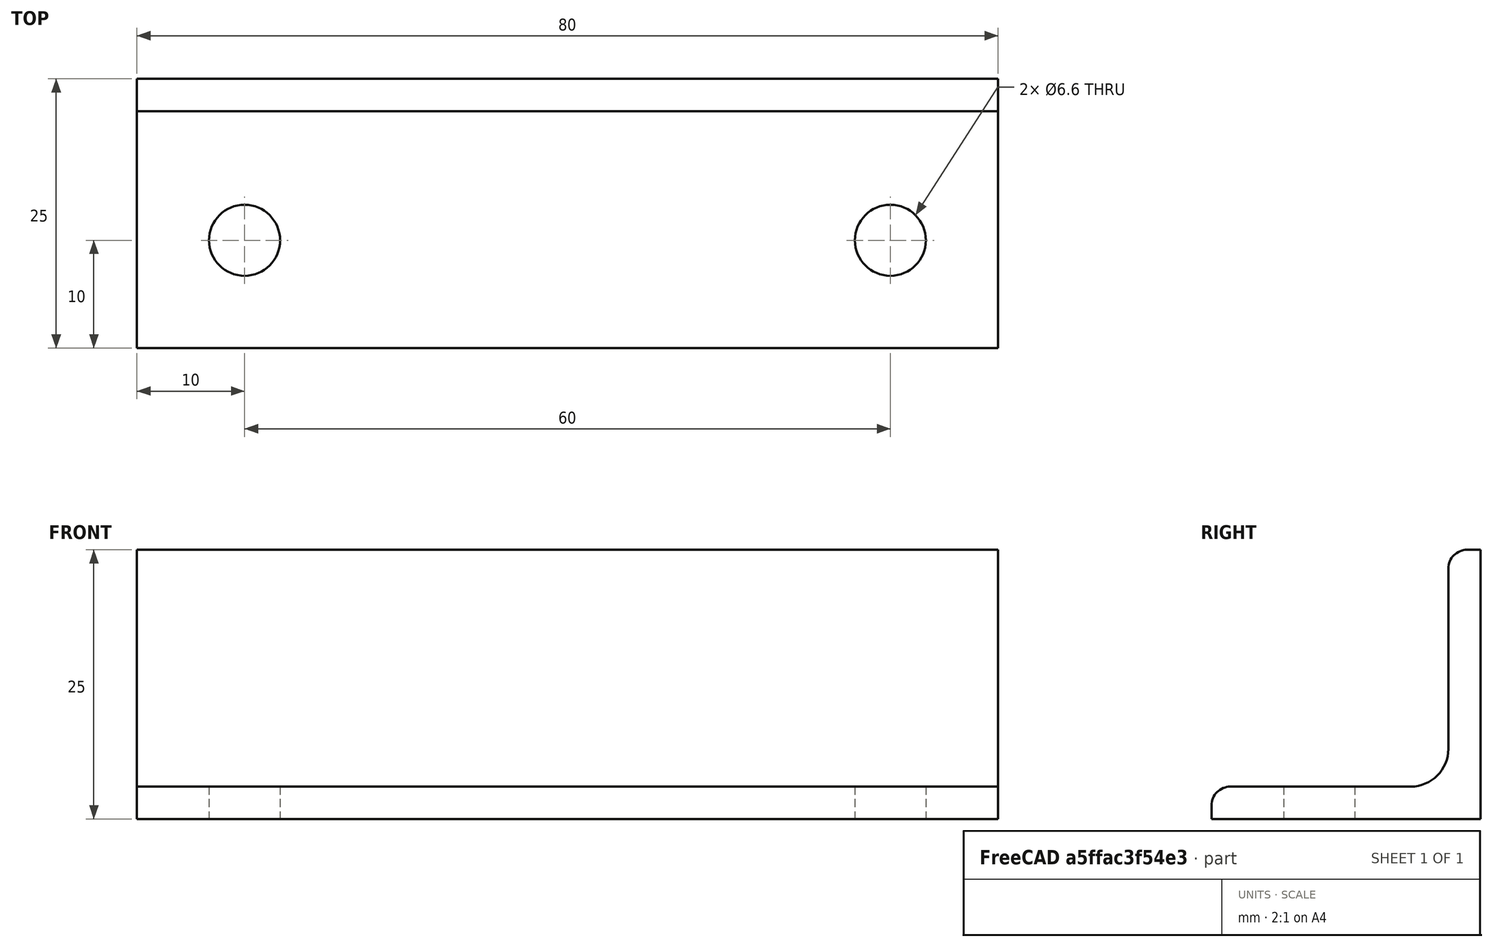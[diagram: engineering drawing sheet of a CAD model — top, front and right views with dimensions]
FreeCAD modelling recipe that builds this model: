
FCSTD DOCUMENT  (FreeCAD 1.0R39319 (Git))
Label: OCT-CHBRA-AC
License: Creative Commons Attribution 4.0
LicenseURL: https://creativecommons.org/licenses/by/4.0/
objects: TechDraw::DrawViewDimension×9, TechDraw::DrawProjGroupItem×3, Sketcher::SketchObject×2, PartDesign::Pad×1, PartDesign::Hole×1, PartDesign::Body×1, TechDraw::DrawSVGTemplate×1, TechDraw::DrawProjGroup×1, TechDraw::DrawPage×1
note: 25 computed .brp shape members not serialized (recipe doc carries the construction recipe); baked Part::Feature solids carry a one-line shape summary decoded from their .brp

FEATURE [Sketcher::SketchObject] Sketch
  ArcFitTolerance = 1e-06
  AttachmentSupport = -> [YZ_Plane001]
  FullyConstrained = true
  MakeInternals = false
  MapMode = 5
  Placement = pos=(0,0,0) rot=(0.57735,0.57735,0.57735;2.0944rad)
  sketch-geometry (9):
    g0: LineSegment StartX=0 StartY=25 StartZ=0 EndX=0 EndY=0 EndZ=0
    g1: LineSegment StartX=0 StartY=0 StartZ=0 EndX=-25 EndY=0 EndZ=0
    g2: ArcOfCircle CenterX=-6.5 CenterY=6.5 CenterZ=0 NormalX=0 NormalY=0 NormalZ=1 AngleXU=0 Radius=3.5 StartAngle=4.71239 EndAngle=6.28319
    g3: LineSegment StartX=-23.25 StartY=3 StartZ=0 EndX=-6.5 EndY=3 EndZ=0
    g4: LineSegment StartX=-3 StartY=6.5 StartZ=0 EndX=-3 EndY=23.25 EndZ=0
    g5: LineSegment StartX=0 StartY=25 StartZ=0 EndX=-1.25 EndY=25 EndZ=0
    g6: ArcOfCircle CenterX=-1.25 CenterY=23.25 CenterZ=0 NormalX=0 NormalY=0 NormalZ=1 AngleXU=0 Radius=1.75 StartAngle=1.5708 EndAngle=3.14159
    g7: LineSegment StartX=-25 StartY=0 StartZ=0 EndX=-25 EndY=1.25 EndZ=0
    g8: ArcOfCircle CenterX=-23.25 CenterY=1.25 CenterZ=0 NormalX=0 NormalY=0 NormalZ=1 AngleXU=0 Radius=1.75 StartAngle=1.5708 EndAngle=3.14159
  constraints (23):
    c: PointOnObject(g0,g-2)
    c: Coincident(g0,g-1)
    c: Coincident(g0,g1)
    c: PointOnObject(g1,g-1)
    c: Vertical(g4)
    c: Horizontal(g3)
    c: Tangent(g3,g2) = -1.5708
    c: Tangent(g4,g2) = -1.5708
    c: DistanceY(g0,g0) = 25
    c: Equal(g0,g1)
    c: Radius(g2) = 3.5
    c: Coincident(g0,g5)
    c: Horizontal(g5)
    c: Tangent(g5,g6) = -1.5708
    c: Coincident(g1,g7)
    c: Vertical(g7)
    c: Tangent(g7,g8) = 1.5708
    c: Tangent(g8,g3) = 1.5708
    c: Tangent(g6,g4) = 1.5708
    c: DistanceX(g4,g0) = 3
    c: Radius(g6) = 1.75
    c: Equal(g8,g6)
    c: Equal(g7,g5)
FEATURE [PartDesign::Pad] Pad
  Direction = (1,0,0)
  Length = 80
  Length2 = 10
  Midplane = true
  Placement = pos=(0,0,0) rot=(1,1,1;2.0944rad)
  Profile = -> Sketch
  ReferenceAxis = -> Sketch [N_Axis]
  Suppressed = false
  Type = 0
FEATURE [Sketcher::SketchObject] Sketch001
  ArcFitTolerance = 1e-06
  AttachmentSupport = -> [Pad]
  FullyConstrained = true
  MakeInternals = false
  MapMode = 5
  Placement = pos=(0,7e-16,3) rot=(0,0,-1;1.5708rad)
  sketch-geometry (2):
    g0: Circle CenterX=15 CenterY=30 CenterZ=0 NormalX=0 NormalY=0 NormalZ=1 AngleXU=0 Radius=3
    g1: Circle CenterX=15 CenterY=-30 CenterZ=0 NormalX=0 NormalY=0 NormalZ=1 AngleXU=0 Radius=3
  constraints (5):
    c: Equal(g0,g1)
    c: Diameter(g0) = 6
    c: Distance(g0,g-2) = 15
    c: Symmetric(g0,g1,g-1)
    c: DistanceY(g1,g0) = 60
FEATURE [PartDesign::Hole] Hole
  BaseFeature = -> Pad
  CustomThreadClearance = 0
  Depth = 176.678
  DepthType = 1
  Diameter = 6.6
  DrillForDepth = false
  DrillPoint = 1
  DrillPointAngle = 118
  HoleCutCountersinkAngle = 90
  HoleCutCustomValues = false
  HoleCutDepth = 0
  HoleCutDiameter = 6.1
  HoleCutType = 0
  ModelThread = false
  Placement = pos=(0,0,0) rot=(1,1,1;2.0944rad)
  Profile = -> Sketch001
  Suppressed = false
  Tapered = false
  TaperedAngle = 90
  ThreadClass = 0
  ThreadDepth = 176.678
  ThreadDepthType = 0
  ThreadDirection = 0
  ThreadFit = 0
  ThreadSize = 14
  ThreadType = 1
  Threaded = false
  UseCustomThreadClearance = false
FEATURE [PartDesign::Body] Body001  label="OCT-CHBRA-AC"
  AllowCompound = false
  Group = -> [Sketch,Pad,Sketch001,Hole]
  Origin = -> Origin001
  Tip = -> Hole
FEATURE [TechDraw::DrawSVGTemplate] Template
  EditableTexts = approval_person=S. Aphelion; creator=Michael Stoll; date_of_issue=22/02/2026; document_status=In preparation; document_type=Component Drawing; drawing_number=DN; general_tolerances=ISO 2768-m; language_code=EN; part_material=Mild Steel S235 / S275; responsible_department=RD; revision_index=A; scale=2 : 1; sheet_number=1 / 1; supplementary_title_1=Chamber Brace; title=OCT-CHBRA-AC
  Height = 297
  Orientation = 1
  Template = C:/Program Files/FreeCAD 1.0/data/Mod/TechDraw/Templates/A3_Landscape_ISO5457_advanced.svg
  Width = 420
FEATURE [TechDraw::DrawProjGroupItem] View  label="Front"
  CoarseView = false
  Direction = (0,0,1)
  Focus = 100
  HardHidden = false
  IsoCount = 0
  IsoHidden = false
  IsoVisible = false
  LockPosition = true
  Perspective = false
  Rotation = 0
  RotationVector = (1,0,0)
  Scale = 2
  ScaleType = 2
  ScrubCount = 1
  SeamHidden = false
  SeamVisible = false
  SmoothHidden = false
  SmoothVisible = true
  Source = -> [Body001]
  Type = 0
  X = 0
  XDirection = (1,0,0)
  Y = 0
FEATURE [TechDraw::DrawProjGroupItem] ProjItem  label="Right"
  CoarseView = false
  Direction = (1,0,1e-16)
  Focus = 100
  HardHidden = false
  IsoCount = 0
  IsoHidden = false
  IsoVisible = false
  LockPosition = false
  Perspective = false
  Rotation = 0
  RotationVector = (1,0,0)
  Scale = 2
  ScaleType = 0
  ScrubCount = 1
  SeamHidden = false
  SeamVisible = false
  SmoothHidden = false
  SmoothVisible = true
  Source = -> [Body001]
  Type = 2
  X = 155
  XDirection = (1e-16,0,-1)
  Y = 0
FEATURE [TechDraw::DrawProjGroup] ProjGroup
  Anchor = -> View
  AutoDistribute = true
  LockPosition = false
  ProjectionType = 1
  Rotation = 0
  Scale = 2
  ScaleType = 0
  Source = -> [Body001]
  Views = -> [View,ProjItem]
  X = 163.103
  Y = 179.132
  spacingX = 50
  spacingY = 50
FEATURE [TechDraw::DrawViewDimension] Dimension
  AngleOverride = false
  Arbitrary = false
  ArbitraryTolerances = false
  BoxCorners = (2) [(-25,-25,0),(25,25,0)]
  EqualTolerance = true
  ExtensionAngle = 0
  FormatSpec = %.1f
  FormatSpecOverTolerance = %+.1f
  FormatSpecUnderTolerance = %+.1f
  Inverted = false
  LineAngle = 0
  LockPosition = false
  MeasureType = 1
  OverTolerance = 0
  References2D = -> [ProjItem]
  Rotation = 0
  Scale = 2
  ScaleType = 0
  TheoreticalExact = false
  Type = 1
  UnderTolerance = 0
  X = 0
  Y = 43.5783
FEATURE [TechDraw::DrawViewDimension] Dimension001
  AngleOverride = false
  Arbitrary = false
  ArbitraryTolerances = false
  BoxCorners = (2) [(-25,-25,0),(25,25,0)]
  EqualTolerance = true
  ExtensionAngle = 0
  FormatSpec = %.1f
  FormatSpecOverTolerance = %+.1f
  FormatSpecUnderTolerance = %+.1f
  Inverted = false
  LineAngle = 0
  LockPosition = false
  MeasureType = 1
  OverTolerance = 0
  References2D = -> [ProjItem]
  Rotation = 0
  Scale = 2
  ScaleType = 0
  TheoreticalExact = false
  Type = 2
  UnderTolerance = 0
  X = 36.1701
  Y = 0
FEATURE [TechDraw::DrawViewDimension] Dimension002
  AngleOverride = false
  Arbitrary = false
  ArbitraryTolerances = false
  BoxCorners = (2) [(-25,-25,0),(25,25,0)]
  EqualTolerance = true
  ExtensionAngle = 0
  FormatSpec = %.1f
  FormatSpecOverTolerance = %+.1f
  FormatSpecUnderTolerance = %+.1f
  Inverted = false
  LineAngle = 0
  LockPosition = false
  MeasureType = 1
  OverTolerance = 0
  References2D = -> [ProjItem]
  Rotation = 0
  Scale = 2
  ScaleType = 0
  TheoreticalExact = false
  Type = 1
  UnderTolerance = 0
  X = 34.6114
  Y = -39.0121
FEATURE [TechDraw::DrawViewDimension] Dimension003
  AngleOverride = false
  Arbitrary = false
  ArbitraryTolerances = false
  BoxCorners = (2) [(-25,-25,0),(25,25,0)]
  EqualTolerance = true
  ExtensionAngle = 0
  FormatSpec = %.1f
  FormatSpecOverTolerance = %+.1f
  FormatSpecUnderTolerance = %+.1f
  Inverted = false
  LineAngle = 0
  LockPosition = false
  MeasureType = 1
  OverTolerance = 0
  References2D = -> [ProjItem]
  Rotation = 0
  Scale = 2
  ScaleType = 0
  TheoreticalExact = false
  Type = 2
  UnderTolerance = 0
  X = -46.1923
  Y = 22
FEATURE [TechDraw::DrawViewDimension] Dimension004
  AngleOverride = false
  Arbitrary = false
  ArbitraryTolerances = false
  BoxCorners = (2) [(-80,-25,-1e-07),(80,25,1e-07)]
  EqualTolerance = true
  ExtensionAngle = 0
  FormatSpec = %.1f
  FormatSpecOverTolerance = %+.1f
  FormatSpecUnderTolerance = %+.1f
  Inverted = false
  LineAngle = 0
  LockPosition = false
  MeasureType = 1
  OverTolerance = 0
  References2D = -> [View]
  Rotation = 0
  Scale = 2
  ScaleType = 0
  TheoreticalExact = false
  Type = 0
  UnderTolerance = 0
  X = -100.804
  Y = 10
FEATURE [TechDraw::DrawViewDimension] Dimension005
  AngleOverride = false
  Arbitrary = false
  ArbitraryTolerances = false
  BoxCorners = (2) [(-80,-25,-1e-07),(80,25,1e-07)]
  EqualTolerance = true
  ExtensionAngle = 0
  FormatSpec = %.1f
  FormatSpecOverTolerance = %+.1f
  FormatSpecUnderTolerance = %+.1f
  Inverted = false
  LineAngle = 0
  LockPosition = false
  MeasureType = 1
  OverTolerance = 0
  References2D = -> [View]
  Rotation = 0
  Scale = 2
  ScaleType = 0
  TheoreticalExact = false
  Type = 1
  UnderTolerance = 0
  X = 0
  Y = -41.2342
FEATURE [TechDraw::DrawViewDimension] Dimension006
  AngleOverride = false
  Arbitrary = false
  ArbitraryTolerances = false
  BoxCorners = (2) [(-80,-25,-1e-07),(80,25,1e-07)]
  EqualTolerance = true
  ExtensionAngle = 0
  FormatSpec = ⌀%.1f
  FormatSpecOverTolerance = %+.1f
  FormatSpecUnderTolerance = %+.1f
  Inverted = false
  LineAngle = 0
  LockPosition = false
  MeasureType = 1
  OverTolerance = 0
  References2D = -> [View]
  Rotation = 0
  Scale = 2
  ScaleType = 0
  TheoreticalExact = false
  Type = 5
  UnderTolerance = 0
  X = -109.355
  Y = -27.5037
FEATURE [TechDraw::DrawViewDimension] Dimension007
  AngleOverride = false
  Arbitrary = false
  ArbitraryTolerances = false
  BoxCorners = (2) [(-80,-25,-1e-07),(80,25,1e-07)]
  EqualTolerance = true
  ExtensionAngle = 0
  FormatSpec = %.1f
  FormatSpecOverTolerance = %+.1f
  FormatSpecUnderTolerance = %+.1f
  Inverted = false
  LineAngle = 0
  LockPosition = false
  MeasureType = 1
  OverTolerance = 0
  References2D = -> [View]
  Rotation = 0
  Scale = 2
  ScaleType = 0
  TheoreticalExact = false
  Type = 1
  UnderTolerance = 0
  X = -70
  Y = -41.2342
FEATURE [TechDraw::DrawViewDimension] Dimension008
  AngleOverride = false
  Arbitrary = false
  ArbitraryTolerances = false
  BoxCorners = (2) [(-80,-25,-1e-07),(80,25,1e-07)]
  EqualTolerance = true
  ExtensionAngle = 0
  FormatSpec = %.1f
  FormatSpecOverTolerance = %+.1f
  FormatSpecUnderTolerance = %+.1f
  Inverted = false
  LineAngle = 0
  LockPosition = false
  MeasureType = 1
  OverTolerance = 0
  References2D = -> [View]
  Rotation = 0
  Scale = 2
  ScaleType = 0
  TheoreticalExact = false
  Type = 1
  UnderTolerance = 0
  X = 0
  Y = 51.5033
FEATURE [TechDraw::DrawProjGroupItem] View001
  CoarseView = false
  Direction = (0.510252,-0.671622,0.537184)
  Focus = 100
  HardHidden = false
  IsoCount = 0
  IsoHidden = false
  IsoVisible = false
  LockPosition = false
  Perspective = false
  Rotation = 0
  RotationVector = (1,0,0)
  ScaleType = 2
  ScrubCount = 1
  SeamHidden = false
  SeamVisible = false
  SmoothHidden = false
  SmoothVisible = true
  Source = -> [Body001]
  Type = 0
  X = 71.7727
  XDirection = (0.810971,0.583679,-0.0405601)
  Y = 54.2361
FEATURE [TechDraw::DrawPage] Page
  KeepUpdated = true
  NextBalloonIndex = 1
  ProjectionType = 1
  Scale = 2
  Template = -> Template
  Views = -> [ProjGroup,Dimension,Dimension001,Dimension002,Dimension003,Dimension004,Dimension005,Dimension006,Dimension007,Dimension008,View001]
